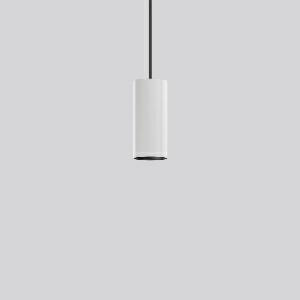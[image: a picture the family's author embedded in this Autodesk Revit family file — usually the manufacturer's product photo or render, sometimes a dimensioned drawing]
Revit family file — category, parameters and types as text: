
# Revit family: deecos_p_mini_911523_002_3_3a1f
name_source: partatom
category: Lighting Fixtures
units: mm (PartAtom-declared; Revit-internal decimal feet)

## family parameters
Cut with Voids When Loaded = No
Host = Face
Light Source = No
Part Type = Normal
Room Calculation Point = No
Round Connector Dimension = Use Diameter
Shared = No

## types (1)
- DEECOS P mini (1 x LED Modul 935, 3800 lm, 3500)
    Apparent Load = 29 VA
    Approval mark = CE
    CIE Flux Codes = 95 99 100 100 100
    Color Rendering = 92
    Color Temperature = 3500
    Default Elevation = 1800 mm
    Description = Series: DEECOS P mini
Cylindrical pendant luminaire. Housing: die-cast aluminium, powder-coated. Canopy made of powder-coated sheet steel with magnetic attachment. Optical assembly with reflector made of MIRO-Silver with 98% total light reflection for outstanding efficiency - can be changed without tools. Best colour rendering index Ra>90. Transparent pendant cable 5 m, can be shortened, with integrated steel cable. High quality converter without flickering and stroboscopic effect. The following accessories can be mounted without use of tools: interchangeable lenses, honeycomb louvre, clear and frosted diffusers, white interchangeable plastic ring. Decorative recessed suspension set available as accessory.Suitable for accessory Deecos P Tube cylinder extensions 0.5 m, 0.75 m or 1 m. 
Colour: traffic white, matt (RAL 9016)
Diameter: 87 mm
Height: 195 mm
Suspension length: 5000 mm
Lamp: LED
Socket: without socket
Colour temperature: 3500K
Colour rendering index (CRI): 92
System power: 29 W
Rated luminous flux: 3800 lm
Luminous efficiency: 131 lm/W
Control gear: Regulated power supply
Protection class: I
Type of protection: IP 20
    Height = 195 mm
    Lamp = 1 x LED Modul 935
    Lamp Light Flux = 3800 lm
    Lamp count = 1
    Length = 87 mm
    Lifetime = 50000 h
    Luminous efficacy = 131 lm/W
    Manufacturer = RZB
    ModVariant = No
    Model = 911523.002.3
    Mounting Place = Ceiling
    Mounting Type = Pendant
    Number of Poles = 1
    OnlyDefault = Yes
    Power Factor = 1
    Product Name = DEECOS P mini
    Product group = Pendant luminaires
    ProductGroupID = 902
    Protection Class = Protection class I
    Protection Degree = IP 20
    RLX_Detail_Level = 1
    RLX_Emergency_Light_Flux = 0 lm
    RLX_Emergency_Type = 0
    RLX_Emergency_Type_DB = No
    RlxData = <blob elided: 54497 chars, md5=26118861>
    Socket = socket
    Standby Power = 0 W
    System Light Flux = 3800 lm
    System Power = 29 W
    Type Comments = Product without accessories
    Type Image = 911476.002.jpg
    URL = http://relux.com
    VarID = ---
    Voltage = 230 V
    Voltage Range = 220-240 V
    Weight = 0.00 kg
    Width = 0 mm  [stored 0 ft]

note: [stored X ft] marks values corroborated as IEEE doubles in the binary element streams (Revit-internal decimal feet)

## geometry (parser evidence)
native form markers: Blend x4, Sweep x14
no freeform markers — native parametric forms only
